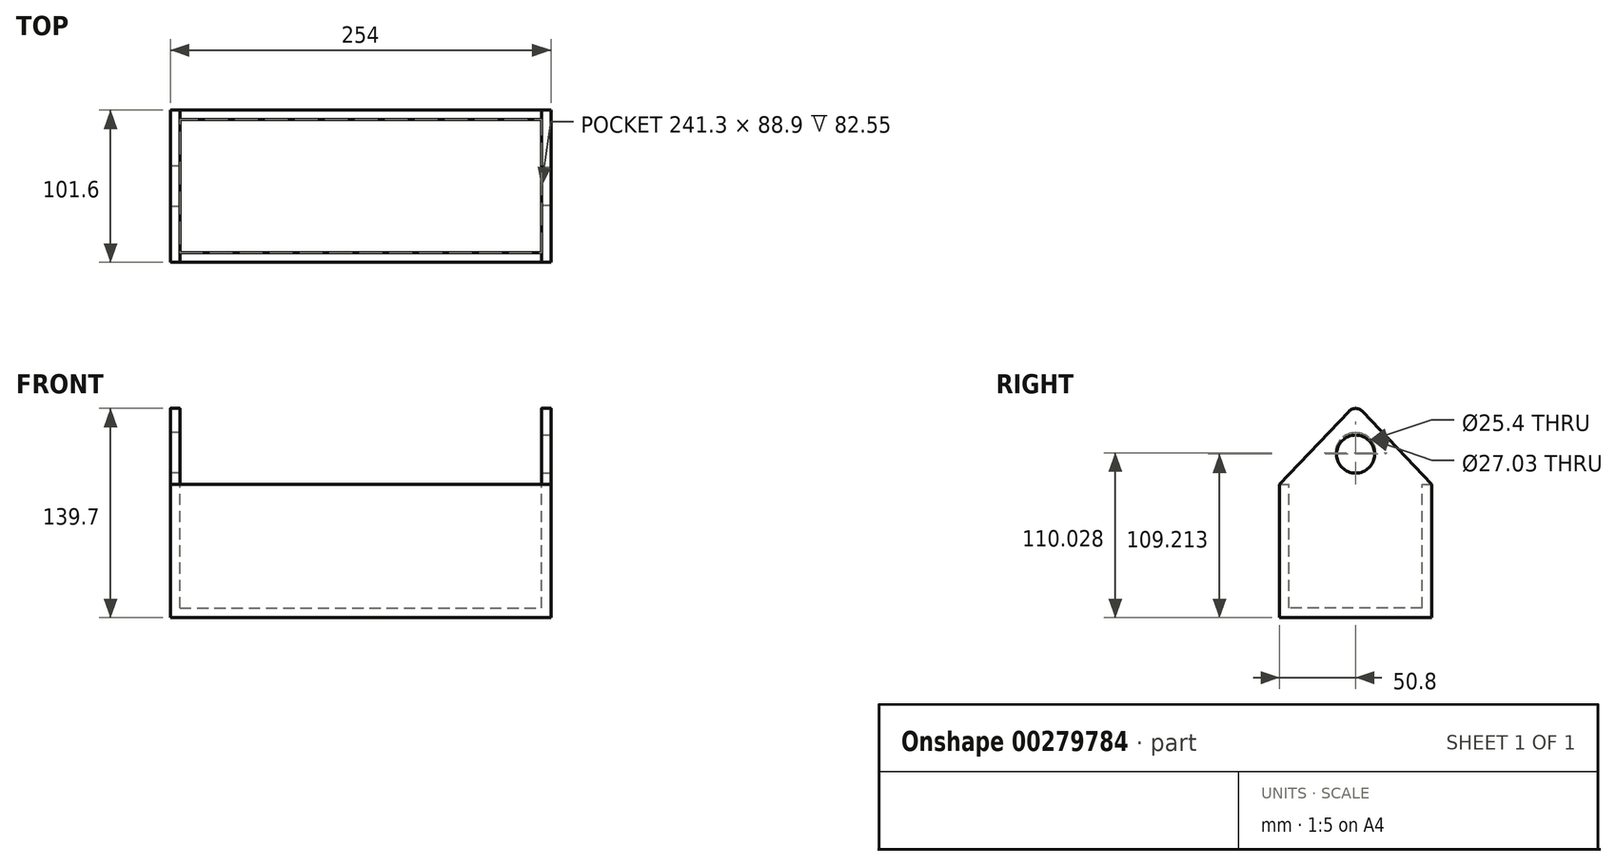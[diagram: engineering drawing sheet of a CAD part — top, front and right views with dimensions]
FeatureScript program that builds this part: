
annotation { "Feature Type Name" : "Feature", "Feature Type Description" : "" }
export const myFeature = defineFeature(function(context is Context, id is Id, definition is map)
    precondition{}
    {
        {
            var Q0;
            Q0=qCreatedBy(makeId("Top.planeOp"),FACE);
            var sketch = newSketch(context, id + "F0", { "sketchPlane" : qUnion([Q0])});
            skLineSegment(sketch, "E0.bottom", {"start": v(-49.65, -23.8) * mm, "end": v(204.35, -23.8) * mm});
            skLineSegment(sketch, "E0.top", {"start": v(-49.65, 77.8) * mm, "end": v(204.35, 77.8) * mm});
            skLineSegment(sketch, "E0.left", {"start": v(-49.65, -23.8) * mm, "end": v(-49.65, 77.8) * mm});
            skLineSegment(sketch, "E0.right", {"start": v(204.35, -23.8) * mm, "end": v(204.35, 77.8) * mm});
            skSolve(sketch);
        }
        {
            var Q0;
            Q0 = qSketchRegion(id + "F0", true);
            extrude(context, id + "F1", {"entities" : qUnion([Q0]), "depth" : 88.9 * mm});
        }
        {
            var Q0;
            Q0=makeQuery(id+"F1.opExtrude","CAP_FACE",FACE,{"disambiguationData":[OSD([sQuery(id+"F0.wireOp",EDGE,"E0.bottom"),sQuery(id+"F0.wireOp",EDGE,"E0.top"),sQuery(id+"F0.wireOp",EDGE,"E0.left"),sQuery(id+"F0.wireOp",EDGE,"E0.right")])],"isStart":false});
            var sketch = newSketch(context, id + "F2", { "sketchPlane" : qUnion([Q0])});
            skLineSegment(sketch, "E1.0", {"start": v(-43.3, -17.45) * mm, "end": v(-43.3, 71.45) * mm});
            skLineSegment(sketch, "E1.1", {"start": v(-43.3, -17.45) * mm, "end": v(198, -17.45) * mm});
            skLineSegment(sketch, "E1.3", {"start": v(-43.3, 71.45) * mm, "end": v(198, 71.45) * mm});
            skLineSegment(sketch, "E2", {"start": v(198, 71.45) * mm, "end": v(198, -17.45) * mm});
            skSolve(sketch);
        }
        {
            var Q0;
            Q0=makeQuery(id+"F1.opExtrude","SWEPT_FACE",FACE,{"disambiguationData":[OSD([sQuery(id+"F0.wireOp",EDGE,"E0.right")])]});
            var sketch = newSketch(context, id + "F3", { "sketchPlane" : qUnion([Q0])});
            skLineSegment(sketch, "E3", {"start": v(-23.8, 88.9) * mm, "end": v(27, 88.9) * mm});
            skLineSegment(sketch, "E4", {"start": v(31.61, 137.71) * mm, "end": v(77.8, 88.9) * mm});
            skLineSegment(sketch, "E5", {"start": v(77.8, 88.9) * mm, "end": v(27, 88.9) * mm});
            skLineSegment(sketch, "E6", {"start": v(22.39, 137.71) * mm, "end": v(-23.8, 88.9) * mm});
            skPoint(sketch, "E7.visualSharp", {"position": v(27, 142.59) * mm});
            skArc(sketch, "E7.filletArc", {"start": v(31.61, 137.71) * mm, "mid": v(27, 139.7) * mm, "end": v(22.39, 137.71) * mm});
            skLineSegment(sketch, "E8", {"start": v(27, 139.7) * mm, "end": v(27, 88.9) * mm});
            skSolve(sketch);
        }
        {
            var Q0;
            Q0 = qSketchRegion(id + "F3", true);
            extrude(context, id + "F4", {"entities" : qUnion([Q0]), "oppositeDirection" : true, "depth" : 6.35 * mm});
        }
        {
            var Q0;
            Q0=makeQuery(id+"F1.opExtrude","CAP_FACE",FACE,{"disambiguationData":[OSD([sQuery(id+"F0.wireOp",EDGE,"E0.bottom"),sQuery(id+"F0.wireOp",EDGE,"E0.top"),sQuery(id+"F0.wireOp",EDGE,"E0.left"),sQuery(id+"F0.wireOp",EDGE,"E0.right")])],"isStart":false});
            var sketch = newSketch(context, id + "F5", { "sketchPlane" : qUnion([Q0])});
            skLineSegment(sketch, "E9", {"start": v(77.35, -17.45) * mm, "end": v(77.35, 71.45) * mm});
            skSolve(sketch);
        }
        {
            var Q0;
            Q0=sQuery(id+"F5.wireOp",EDGE,"E9");
            extrude(context, id + "F6", {"bodyType" : ToolBodyType.SURFACE, "operationType" : NewBodyOperationType.ADD, "surfaceEntities" : qUnion([Q0]), "endBound" : BoundingType.SYMMETRIC, "depth" : 0.25 * mm});
        }
        {
            var Q0;
            Q0=makeQuery(id+"F4.opExtrude","SWEPT_BODY",BODY,{"disambiguationData":[OSD([sQuery(id+"F3.wireOp",EDGE,"E3"),sQuery(id+"F3.wireOp",EDGE,"E4"),sQuery(id+"F3.wireOp",EDGE,"E5"),sQuery(id+"F3.wireOp",EDGE,"E6"),sQuery(id+"F3.wireOp",EDGE,"E7.filletArc")])]});
            var Q1;
            Q1=makeQuery(id+"F6.opExtrude","SWEPT_FACE",FACE,{"disambiguationData":[OSD([sQuery(id+"F5.wireOp",EDGE,"E9")])]});
            mirror(context, id + "F7", {"operationType" : NewBodyOperationType.ADD, "entities" : qUnion([Q0]), "mirrorPlane" : qUnion([Q1])});
        }
        {
            var Q0;
            Q0=makeQuery(id+"F2.imprint","IMPRINT",FACE,{"disambiguationData":[TD([[makeQuery(id+"F2.imprint","IMPRINT",EDGE,{"derivedFrom":sQuery(id+"F2.wireOp",EDGE,"E1.0")}),-1.0]])]});
            extrude(context, id + "F8", {"entities" : qUnion([Q0]), "operationType" : NewBodyOperationType.REMOVE, "oppositeDirection" : true, "depth" : 82.55 * mm});
        }
        {
            var Q0;
            Q0=makeQuery(id+"F7.boolean.opBoolean","MERGE",FACE,{"derivedFrom":[makeQuery(id+"F1.opExtrude","SWEPT_FACE",FACE,{"disambiguationData":[OSD([sQuery(id+"F0.wireOp",EDGE,"E0.right")])]}),makeQuery(id+"F4.opExtrude","CAP_FACE",FACE,{"disambiguationData":[OSD([sQuery(id+"F3.wireOp",EDGE,"E3"),sQuery(id+"F3.wireOp",EDGE,"E4"),sQuery(id+"F3.wireOp",EDGE,"E5"),sQuery(id+"F3.wireOp",EDGE,"E6"),sQuery(id+"F3.wireOp",EDGE,"E7.filletArc")])],"isStart":true})]});
            var sketch = newSketch(context, id + "F9", { "sketchPlane" : qUnion([Q0])});
            skCircle(sketch, "E10", {"center": v(27, 109.21) * mm, "radius": 12.7 * mm});
            skPoint(sketch, "E10.centerSnap0", {"position": v(27, 139.7) * mm});
            skSolve(sketch);
        }
        {
            var Q0;
            Q0=makeQuery(id+"F9.imprint","IMPRINT",FACE,{"disambiguationData":[TD([[makeQuery(id+"F9.imprint","IMPRINT",EDGE,{"derivedFrom":sQuery(id+"F9.wireOp",EDGE,"E10")}),1.0]])]});
            extrude(context, id + "F10", {"entities" : qUnion([Q0]), "operationType" : NewBodyOperationType.REMOVE, "oppositeDirection" : true, "depth" : 25.4 * mm});
        }
        {
            var Q0;
            Q0=makeQuery(id+"F7.boolean.opBoolean","MERGE",FACE,{"derivedFrom":[makeQuery(id+"F1.opExtrude","SWEPT_FACE",FACE,{"disambiguationData":[OSD([sQuery(id+"F0.wireOp",EDGE,"E0.left")])]}),makeQuery(id+"F7.opPattern","COPY",FACE,{"derivedFrom":makeQuery(id+"F4.opExtrude","CAP_FACE",FACE,{"disambiguationData":[OSD([sQuery(id+"F3.wireOp",EDGE,"E3"),sQuery(id+"F3.wireOp",EDGE,"E4"),sQuery(id+"F3.wireOp",EDGE,"E5"),sQuery(id+"F3.wireOp",EDGE,"E6"),sQuery(id+"F3.wireOp",EDGE,"E7.filletArc")])],"isStart":true}),"instanceName":"1"})]});
            var sketch = newSketch(context, id + "F11", { "sketchPlane" : qUnion([Q0])});
            skCircle(sketch, "E11", {"center": v(-27, 110.03) * mm, "radius": 13.52 * mm});
            skPoint(sketch, "E11.centerSnap0", {"position": v(-27, 139.7) * mm});
            skSolve(sketch);
        }
        {
            var Q0;
            Q0 = qSketchRegion(id + "F11", true);
            extrude(context, id + "F12", {"entities" : qUnion([Q0]), "operationType" : NewBodyOperationType.REMOVE, "oppositeDirection" : true, "depth" : 25.4 * mm});
        }
    });
